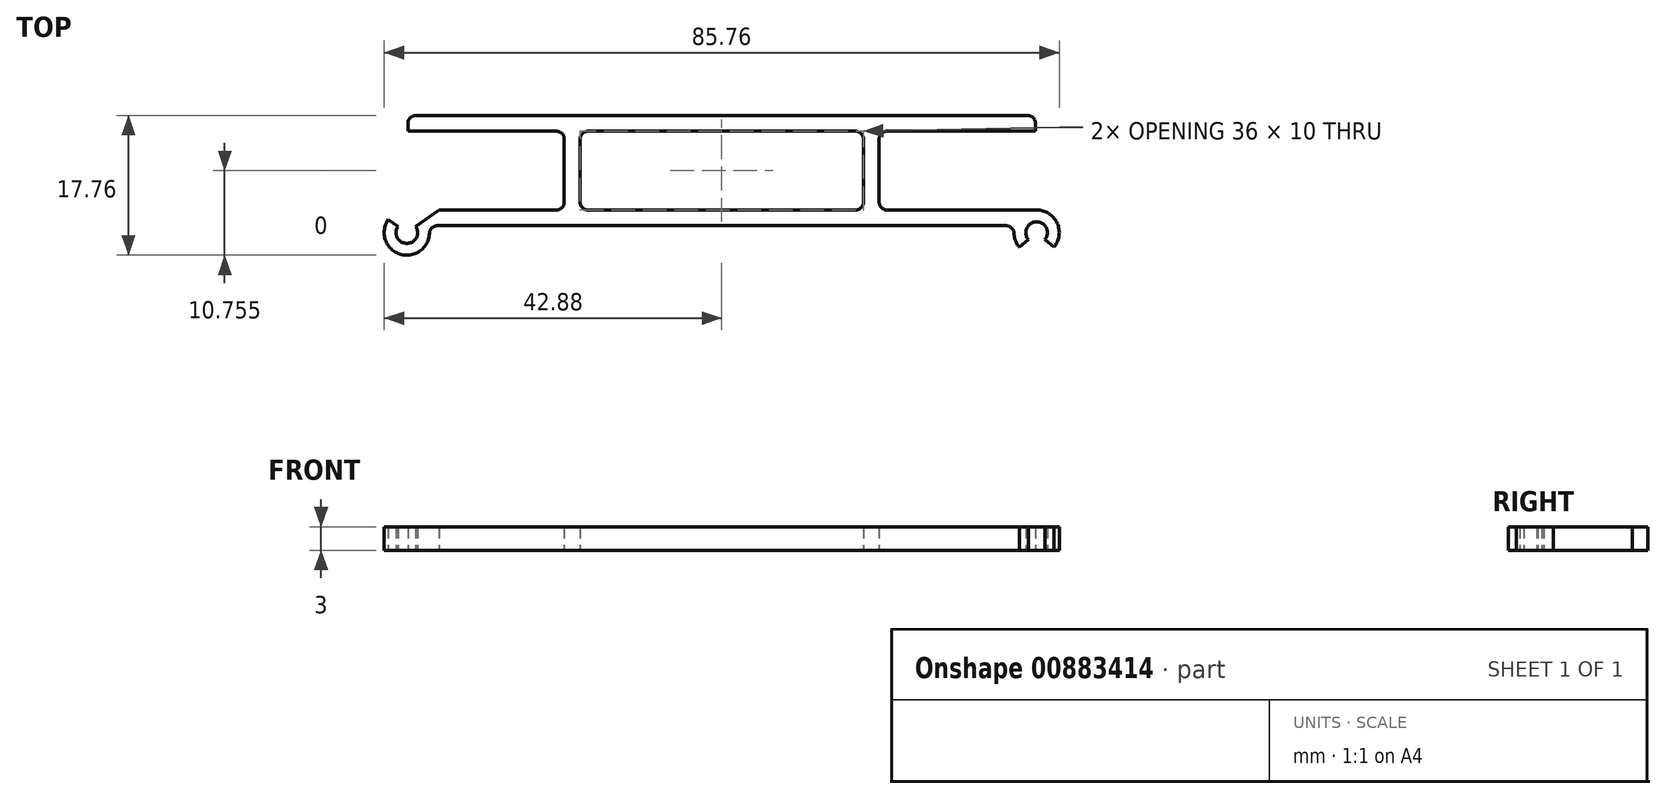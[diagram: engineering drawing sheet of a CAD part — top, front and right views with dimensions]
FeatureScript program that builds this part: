
annotation { "Feature Type Name" : "Feature", "Feature Type Description" : "" }
export const myFeature = defineFeature(function(context is Context, id is Id, definition is map)
    precondition{}
    {
        {
            var Q0;
            Q0=qCreatedBy(makeId("Top.planeOp"),FACE);
            var sketch = newSketch(context, id + "F0", { "sketchPlane" : qUnion([Q0])});
            skArc(sketch, "E0", {"start": v(-38.95, -0.88) * mm, "mid": v(-38.63, -0.06) * mm, "end": v(-38.87, 0.79) * mm});
            skArc(sketch, "E1", {"start": v(-37.8, -1.85) * mm, "mid": v(-37.31, -1.03) * mm, "end": v(-37.13, -0.1) * mm});
            skLineSegment(sketch, "E2", {"start": v(-40, 0) * mm, "end": v(-40, 8.28) * mm, "construction": true});
            skLineSegment(sketch, "E3", {"start": v(-40, 8.28) * mm, "end": v(-40, -12.34) * mm, "construction": true});
            skLineSegment(sketch, "E4", {"start": v(-35.9, 2.88) * mm, "end": v(-21, 2.88) * mm});
            skLineSegment(sketch, "E5", {"start": v(-36.13, 0.88) * mm, "end": v(0, 0.88) * mm});
            skLineSegment(sketch, "E6.right", {"start": v(-20, 11.88) * mm, "end": v(-20, 3.88) * mm});
            skLineSegment(sketch, "E7.bottom", {"start": v(-21, 12.88) * mm, "end": v(-39.87, 12.87) * mm});
            skLineSegment(sketch, "E7.top", {"start": v(0.13, 14.88) * mm, "end": v(-38.87, 14.88) * mm});
            skLineSegment(sketch, "E7.right", {"start": v(-39.87, 12.87) * mm, "end": v(-39.87, 13.87) * mm});
            skPoint(sketch, "E8.orphan", {"position": v(0, 2.88) * mm});
            skPoint(sketch, "E7.left.start.orphan", {"position": v(0, 12.88) * mm});
            skLineSegment(sketch, "E9.MirrorCS", {"start": v(39.87, 12.87) * mm, "end": v(39.87, 13.88) * mm});
            skArc(sketch, "E10.MirrorCS", {"start": v(38.95, -0.88) * mm, "mid": v(40, 1.38) * mm, "end": v(41.05, -0.88) * mm});
            skLineSegment(sketch, "E11.MirrorCS", {"start": v(36.13, 0.88) * mm, "end": v(0, 0.88) * mm});
            skLineSegment(sketch, "E12.MirrorCS", {"start": v(40, 2.87) * mm, "end": v(21, 2.88) * mm});
            skLineSegment(sketch, "E13.MirrorCS", {"start": v(40, 0) * mm, "end": v(40, 8.28) * mm, "construction": true});
            skLineSegment(sketch, "E14.MirrorCS", {"start": v(20, 11.88) * mm, "end": v(20, 3.88) * mm});
            skLineSegment(sketch, "E15.MirrorCS", {"start": v(-0.13, 14.88) * mm, "end": v(38.87, 14.88) * mm});
            skLineSegment(sketch, "E16.MirrorCS", {"start": v(21, 12.88) * mm, "end": v(39.87, 12.88) * mm});
            skArc(sketch, "E17.MirrorCS", {"start": v(37.8, -1.85) * mm, "mid": v(37.31, -1.03) * mm, "end": v(37.13, -0.1) * mm});
            skLineSegment(sketch, "E18.MirrorCS", {"start": v(41.05, -0.88) * mm, "end": v(45.35, -4.49) * mm});
            skLineSegment(sketch, "E19.MirrorCS", {"start": v(38.95, -0.88) * mm, "end": v(34.65, -4.49) * mm});
            skArc(sketch, "E20.trimOffspring", {"start": v(-42.36, 1.65) * mm, "mid": v(-42.87, -0.13) * mm, "end": v(-42.2, -1.85) * mm});
            skArc(sketch, "E21.trimOffspring", {"start": v(40, 2.88) * mm, "mid": v(42.6, 1.22) * mm, "end": v(42.2, -1.85) * mm});
            skPoint(sketch, "E22.visualSharp", {"position": v(-39.87, 14.87) * mm});
            skArc(sketch, "E22.filletArc", {"start": v(-38.87, 14.88) * mm, "mid": v(-39.57, 14.58) * mm, "end": v(-39.87, 13.87) * mm});
            skPoint(sketch, "E23.visualSharp", {"position": v(-37.26, 0.88) * mm});
            skArc(sketch, "E23.filletArc", {"start": v(-36.13, 0.88) * mm, "mid": v(-36.82, 0.6) * mm, "end": v(-37.13, -0.1) * mm});
            skPoint(sketch, "E24.visualSharp", {"position": v(-20, 2.88) * mm});
            skArc(sketch, "E24.filletArc", {"start": v(-21, 2.88) * mm, "mid": v(-20.3, 3.17) * mm, "end": v(-20, 3.88) * mm});
            skPoint(sketch, "E25.visualSharp", {"position": v(-20, 12.88) * mm});
            skArc(sketch, "E25.filletArc", {"start": v(-20, 11.88) * mm, "mid": v(-20.3, 12.58) * mm, "end": v(-21, 12.88) * mm});
            skPoint(sketch, "E26.visualSharp", {"position": v(20, 12.88) * mm});
            skArc(sketch, "E26.filletArc", {"start": v(21, 12.88) * mm, "mid": v(20.3, 12.58) * mm, "end": v(20, 11.88) * mm});
            skPoint(sketch, "E27.visualSharp", {"position": v(20, 2.88) * mm});
            skArc(sketch, "E27.filletArc", {"start": v(20, 3.88) * mm, "mid": v(20.3, 3.17) * mm, "end": v(21, 2.88) * mm});
            skPoint(sketch, "E28.visualSharp", {"position": v(37.26, 0.88) * mm});
            skArc(sketch, "E28.filletArc", {"start": v(37.13, -0.1) * mm, "mid": v(36.82, 0.6) * mm, "end": v(36.13, 0.88) * mm});
            skPoint(sketch, "E29.visualSharp", {"position": v(39.87, 14.87) * mm});
            skArc(sketch, "E29.filletArc", {"start": v(39.87, 13.88) * mm, "mid": v(39.57, 14.58) * mm, "end": v(38.87, 14.88) * mm});
            skLineSegment(sketch, "E30.bottom", {"start": v(-17, 12.88) * mm, "end": v(0, 12.88) * mm});
            skLineSegment(sketch, "E30.top", {"start": v(-17, 2.88) * mm, "end": v(0, 2.88) * mm});
            skLineSegment(sketch, "E30.left", {"start": v(-18, 11.88) * mm, "end": v(-18, 3.88) * mm});
            skLineSegment(sketch, "E30.right", {"start": v(0, 12.88) * mm, "end": v(0, 2.88) * mm});
            skPoint(sketch, "E31.visualSharp", {"position": v(-18, 12.88) * mm});
            skArc(sketch, "E31.filletArc", {"start": v(-17, 12.88) * mm, "mid": v(-17.7, 12.58) * mm, "end": v(-18, 11.88) * mm});
            skPoint(sketch, "E32.visualSharp", {"position": v(-18, 2.88) * mm});
            skArc(sketch, "E32.filletArc", {"start": v(-18, 3.88) * mm, "mid": v(-17.7, 3.17) * mm, "end": v(-17, 2.88) * mm});
            skLineSegment(sketch, "E33.MirrorCS", {"start": v(17, 12.88) * mm, "end": v(0, 12.88) * mm});
            skLineSegment(sketch, "E34.MirrorCS", {"start": v(18, 11.88) * mm, "end": v(18, 3.88) * mm});
            skArc(sketch, "E35.MirrorCS", {"start": v(18, 3.88) * mm, "mid": v(17.7, 3.17) * mm, "end": v(17, 2.88) * mm});
            skLineSegment(sketch, "E36.MirrorCS", {"start": v(17, 2.88) * mm, "end": v(0, 2.88) * mm});
            skArc(sketch, "E37.MirrorCS", {"start": v(17, 12.88) * mm, "mid": v(17.7, 12.58) * mm, "end": v(18, 11.88) * mm});
            skArc(sketch, "E38", {"start": v(-41.13, 0.79) * mm, "mid": v(-40, -1.37) * mm, "end": v(-38.87, 0.79) * mm});
            skArc(sketch, "E39", {"start": v(-42.36, 1.65) * mm, "mid": v(-40.9, -2.73) * mm, "end": v(-37.13, -0.1) * mm});
            skLineSegment(sketch, "E40", {"start": v(-40, 0) * mm, "end": v(-44.34, 3.04) * mm, "construction": true});
            skLineSegment(sketch, "E41", {"start": v(-40, 0) * mm, "end": v(-35.84, 2.92) * mm, "construction": true});
            skLineSegment(sketch, "E42", {"start": v(-42.36, 1.65) * mm, "end": v(-41.13, 0.79) * mm});
            skLineSegment(sketch, "E43", {"start": v(-38.87, 0.79) * mm, "end": v(-37.64, 1.65) * mm});
            skLineSegment(sketch, "E44", {"start": v(-37.64, 1.65) * mm, "end": v(-35.84, 2.92) * mm});
            skPoint(sketch, "E45.orphan", {"position": v(-40, 2.88) * mm});
            skArc(sketch, "E46.trimOffspring", {"start": v(-41.13, 0.79) * mm, "mid": v(-41.37, -0.06) * mm, "end": v(-41.05, -0.88) * mm});
            skSolve(sketch);
        }
        {
            var Q0;
            {var subQ9=sQuery(id+"F0.wireOp",EDGE,"E4");Q0=makeQuery(id+"F0.imprint","IMPRINT",FACE,{"disambiguationData":[TD([[makeQuery(id+"F0.imprint","IMPRINT",EDGE,{"derivedFrom":subQ9}),-1.0]])]});}
            extrude(context, id + "F1", {"entities" : qUnion([Q0]), "depth" : 3 * mm, "offsetDistance" : 25 * mm});
        }
    });
